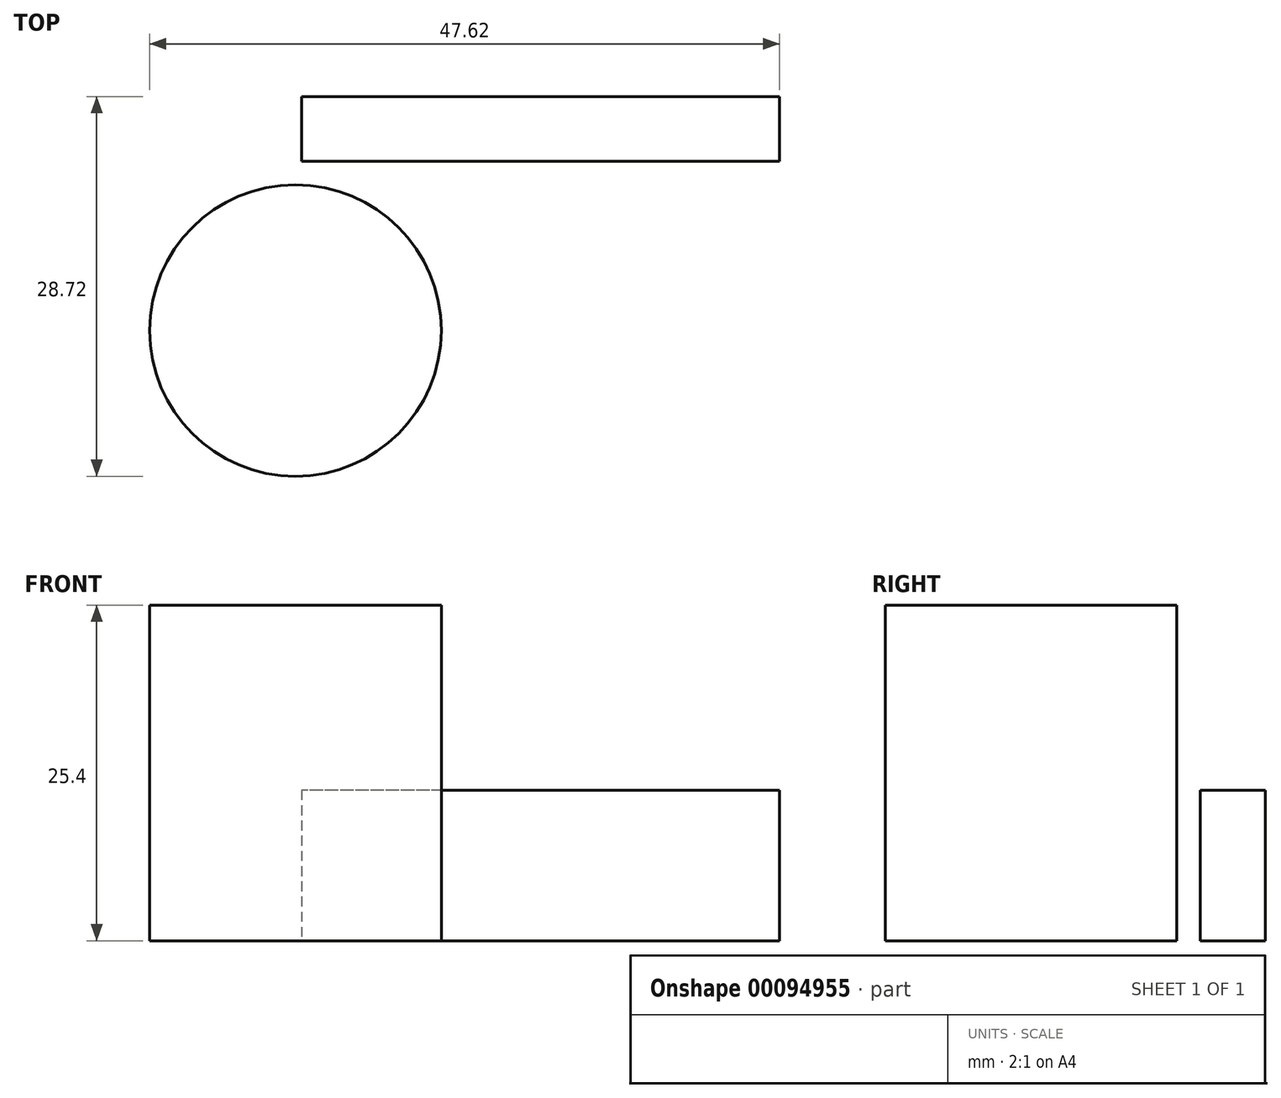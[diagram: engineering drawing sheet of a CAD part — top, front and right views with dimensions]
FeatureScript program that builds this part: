
annotation { "Feature Type Name" : "Feature", "Feature Type Description" : "" }
export const myFeature = defineFeature(function(context is Context, id is Id, definition is map)
    precondition{}
    {
        {
            var Q0;
            Q0=qCreatedBy(makeId("Top.planeOp"),FACE);
            var sketch = newSketch(context, id + "F0", { "sketchPlane" : qUnion([Q0])});
            skLineSegment(sketch, "E0.bottom", {"start": v(0, 0) * mm, "end": v(-36.12, 0) * mm});
            skLineSegment(sketch, "E0.top", {"start": v(0, 4.9) * mm, "end": v(-36.12, 4.9) * mm});
            skLineSegment(sketch, "E0.left", {"start": v(0, 0) * mm, "end": v(0, 4.9) * mm});
            skLineSegment(sketch, "E0.right", {"start": v(-36.12, 0) * mm, "end": v(-36.12, 4.9) * mm});
            skSolve(sketch);
        }
        {
            var Q0;
            Q0 = qSketchRegion(id + "F0", true);
            extrude(context, id + "F1", {"entities" : qUnion([Q0]), "depth" : 11.4 * mm});
        }
        {
            var Q0;
            Q0=qCreatedBy(makeId("Top.planeOp"),FACE);
            var sketch = newSketch(context, id + "F2", { "sketchPlane" : qUnion([Q0])});
            skCircle(sketch, "E1", {"center": v(-36.6, -12.8) * mm, "radius": 11.03 * mm});
            skSolve(sketch);
        }
        {
            var Q0;
            Q0=makeQuery(id+"F2.imprint","IMPRINT",FACE,{"disambiguationData":[TD([[makeQuery(id+"F2.imprint","IMPRINT",EDGE,{"derivedFrom":sQuery(id+"F2.wireOp",EDGE,"E1")}),1.0]])]});
            extrude(context, id + "F3", {"entities" : qUnion([Q0]), "depth" : 25.4 * mm});
        }
    });
